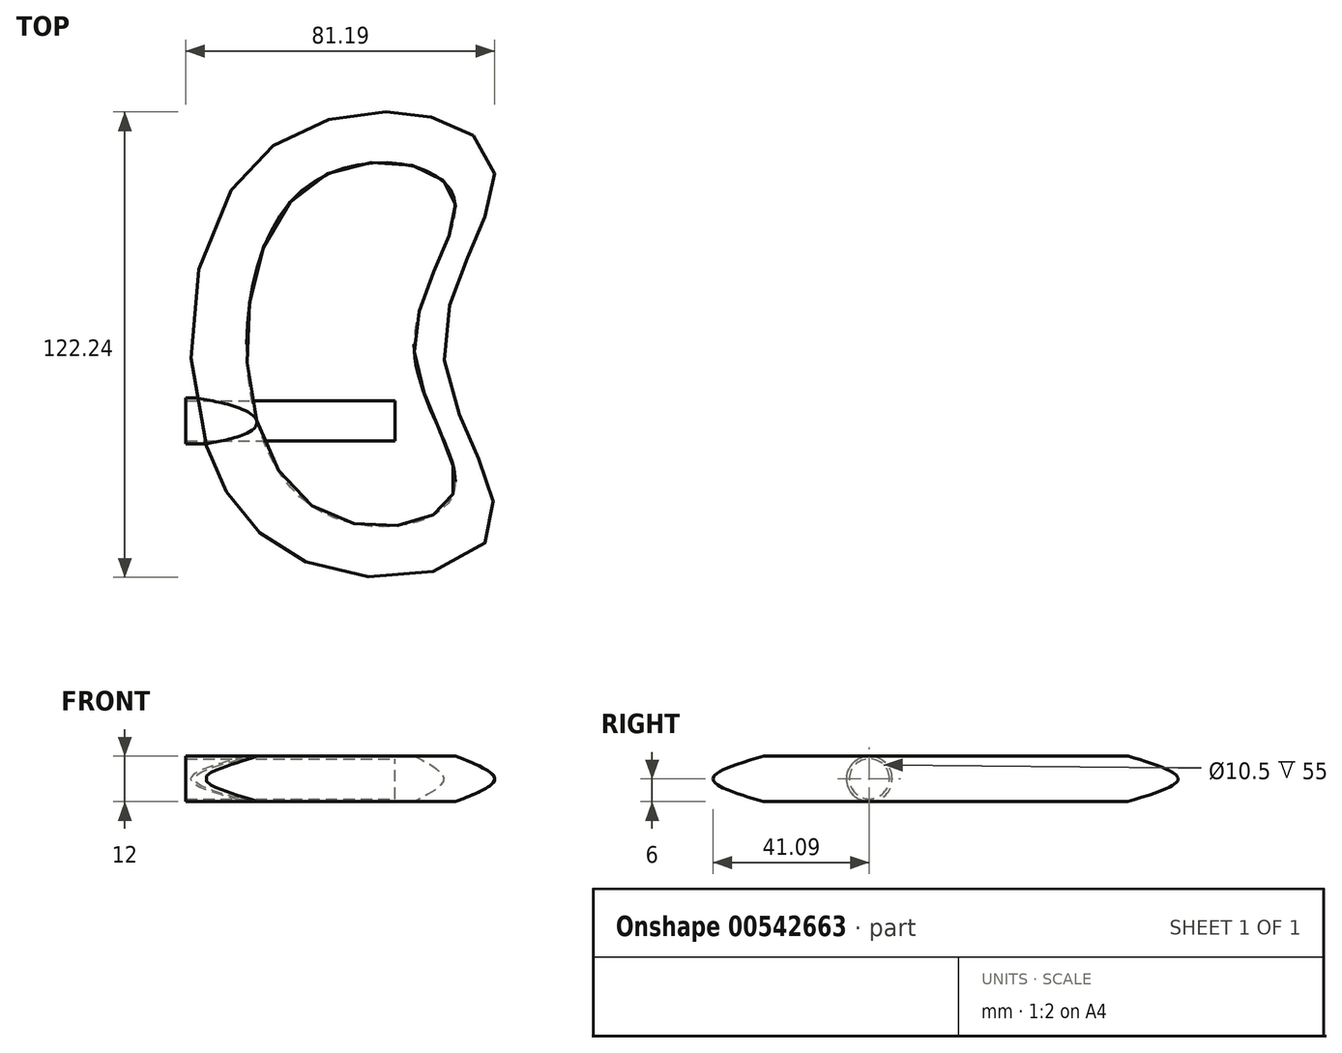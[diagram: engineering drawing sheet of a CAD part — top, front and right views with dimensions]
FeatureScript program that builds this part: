
annotation { "Feature Type Name" : "Feature", "Feature Type Description" : "" }
export const myFeature = defineFeature(function(context is Context, id is Id, definition is map)
    precondition{}
    {
        {
            var Q0;
            Q0=qCreatedBy(makeId("Top.planeOp"),FACE);
            var sketch = newSketch(context, id + "F0", { "sketchPlane" : qUnion([Q0])});
            skFitSpline(sketch, "E0", {"points": [v(0, 40) * mm, v(40, 40) * mm, v(30, 0) * mm, v(40, -40) * mm, v(0, -40) * mm, v(0, 40) * mm]});
            skSolve(sketch);
        }
        {
            var Q0;
            Q0=qCreatedBy(makeId("Top.planeOp"),FACE);
            cPlane(context, id + "F1", {"entities" : qUnion([Q0]), "cplaneType" : CPlaneType.OFFSET, "offset" : 6 * mm, "width" : 150 * mm, "height" : 150 * mm});
        }
        {
            var Q0;
            Q0=qCreatedBy(id+"F1.planeOp",FACE);
            cPlane(context, id + "F2", {"entities" : qUnion([Q0]), "cplaneType" : CPlaneType.OFFSET, "offset" : 6 * mm, "width" : 150 * mm, "height" : 150 * mm});
        }
        {
            var Q0;
            Q0=qCreatedBy(id+"F2.planeOp",FACE);
            var sketch = newSketch(context, id + "F3", { "sketchPlane" : qUnion([Q0])});
            skFitSpline(sketch, "E1", {"points": [v(0, 40.13) * mm, v(40, 40.13) * mm, v(30, 0.13) * mm, v(40, -39.87) * mm, v(0, -39.87) * mm, v(0, 40.13) * mm]});
            skSolve(sketch);
        }
        {
            var Q0;
            Q0=qCreatedBy(id+"F1.planeOp",FACE);
            var sketch = newSketch(context, id + "F4", { "sketchPlane" : qUnion([Q0])});
            skFitSpline(sketch, "E2", {"points": [v(-10, 50) * mm, v(50, 50) * mm, v(37.78, -0.38) * mm, v(50, -50) * mm, v(-10, -50) * mm, v(-10, 50) * mm]});
            skSolve(sketch);
        }
        {
            var Q0;
            Q0=makeQuery(id+"F0.imprint","IMPRINT",FACE,{"disambiguationData":[TD([[makeQuery(id+"F0.imprint","IMPRINT",EDGE,{"derivedFrom":sQuery(id+"F0.wireOp",EDGE,"E0")}),-1.0]])]});
            var Q1;
            Q1=makeQuery(id+"F4.imprint","IMPRINT",FACE,{"disambiguationData":[TD([[makeQuery(id+"F4.imprint","IMPRINT",EDGE,{"derivedFrom":sQuery(id+"F4.wireOp",EDGE,"E2")}),-1.0]])]});
            var Q2;
            Q2=makeQuery(id+"F3.imprint","IMPRINT",FACE,{"disambiguationData":[TD([[makeQuery(id+"F3.imprint","IMPRINT",EDGE,{"derivedFrom":sQuery(id+"F3.wireOp",EDGE,"E1")}),-1.0]])]});
            loft(context, id + "F5", {"sheetProfilesArray" : [{ "sheetProfileEntities" : qUnion([Q0]) }, { "sheetProfileEntities" : qUnion([Q1]) }, { "sheetProfileEntities" : qUnion([Q2]) }]});
        }
        {
            var Q0;
            Q0=qCreatedBy(makeId("Right.planeOp"),FACE);
            var sketch = newSketch(context, id + "F6", { "sketchPlane" : qUnion([Q0])});
            skCircle(sketch, "E3", {"center": v(-20, 6) * mm, "radius": 6 * mm});
            skSolve(sketch);
        }
        {
            var Q0;
            Q0 = qSketchRegion(id + "F6", true);
            extrude(context, id + "F7", {"entities" : qUnion([Q0]), "operationType" : NewBodyOperationType.ADD, "oppositeDirection" : true, "depth" : 30 * mm, "offsetDistance" : 25 * mm});
        }
        {
            var Q0;
            Q0=qCreatedBy(makeId("Right.planeOp"),FACE);
            var sketch = newSketch(context, id + "F8", { "sketchPlane" : qUnion([Q0])});
            skCircle(sketch, "E4", {"center": v(-20, 6) * mm, "radius": 5.25 * mm});
            skSolve(sketch);
        }
        {
            var Q0;
            Q0 = qSketchRegion(id + "F8", true);
            extrude(context, id + "F9", {"entities" : qUnion([Q0]), "operationType" : NewBodyOperationType.REMOVE, "oppositeDirection" : true, "depth" : 30 * mm, "offsetDistance" : 25 * mm, "hasSecondDirection" : true, "secondDirectionOppositeDirection" : false, "secondDirectionDepth" : 25 * mm});
        }
    });
